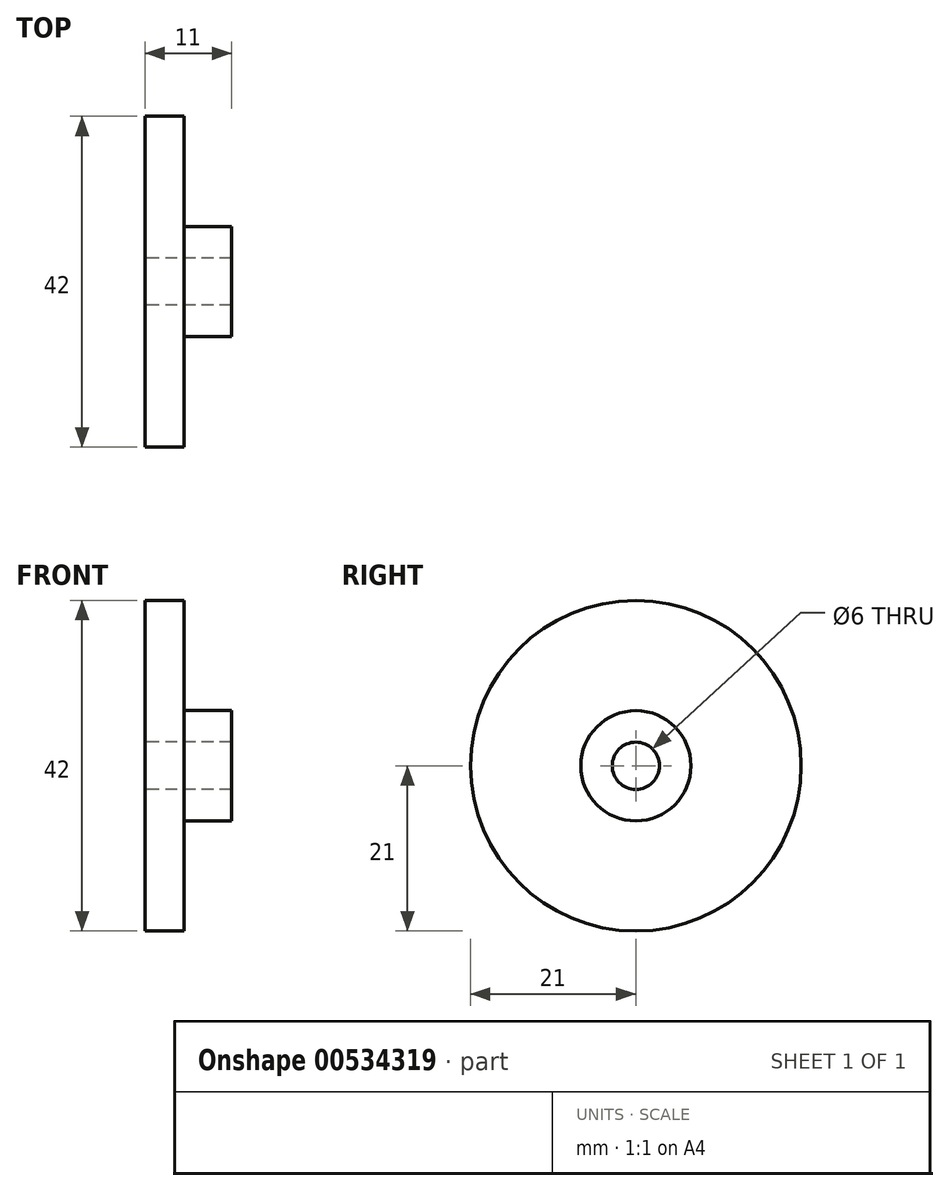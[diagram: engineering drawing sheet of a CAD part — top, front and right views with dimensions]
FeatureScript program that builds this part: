
annotation { "Feature Type Name" : "Feature", "Feature Type Description" : "" }
export const myFeature = defineFeature(function(context is Context, id is Id, definition is map)
    precondition{}
    {
        {
            var Q0;
            Q0=qCreatedBy(makeId("Front.planeOp"),FACE);
            var sketch = newSketch(context, id + "F0", { "sketchPlane" : qUnion([Q0])});
            skLineSegment(sketch, "E0", {"start": v(0, 3) * mm, "end": v(11, 3) * mm});
            skLineSegment(sketch, "E1", {"start": v(11, 3) * mm, "end": v(11, 7) * mm});
            skLineSegment(sketch, "E2", {"start": v(11, 7) * mm, "end": v(5, 7) * mm});
            skLineSegment(sketch, "E3", {"start": v(5, 7) * mm, "end": v(5, 21) * mm});
            skLineSegment(sketch, "E4", {"start": v(5, 21) * mm, "end": v(0, 21) * mm});
            skLineSegment(sketch, "E5", {"start": v(0, 21) * mm, "end": v(0, 3) * mm});
            skSolve(sketch);
        }
        {
            var Q0;
            Q0=qCreatedBy(makeId("Front.planeOp"),FACE);
            var sketch = newSketch(context, id + "F1", { "sketchPlane" : qUnion([Q0])});
            skLineSegment(sketch, "E6", {"start": v(0, 0) * mm, "end": v(50.37, 0) * mm});
            skSolve(sketch);
        }
        {
            var Q0;
            Q0 = qSketchRegion(id + "F0", true);
            var Q1;
            Q1=sQuery(id+"F1.wireOp",EDGE,"E6");
            revolve(context, id + "F2", {"entities" : qUnion([Q0]), "axis" : qUnion([Q1]), "revolveType" : RevolveType.FULL});
        }
    });
